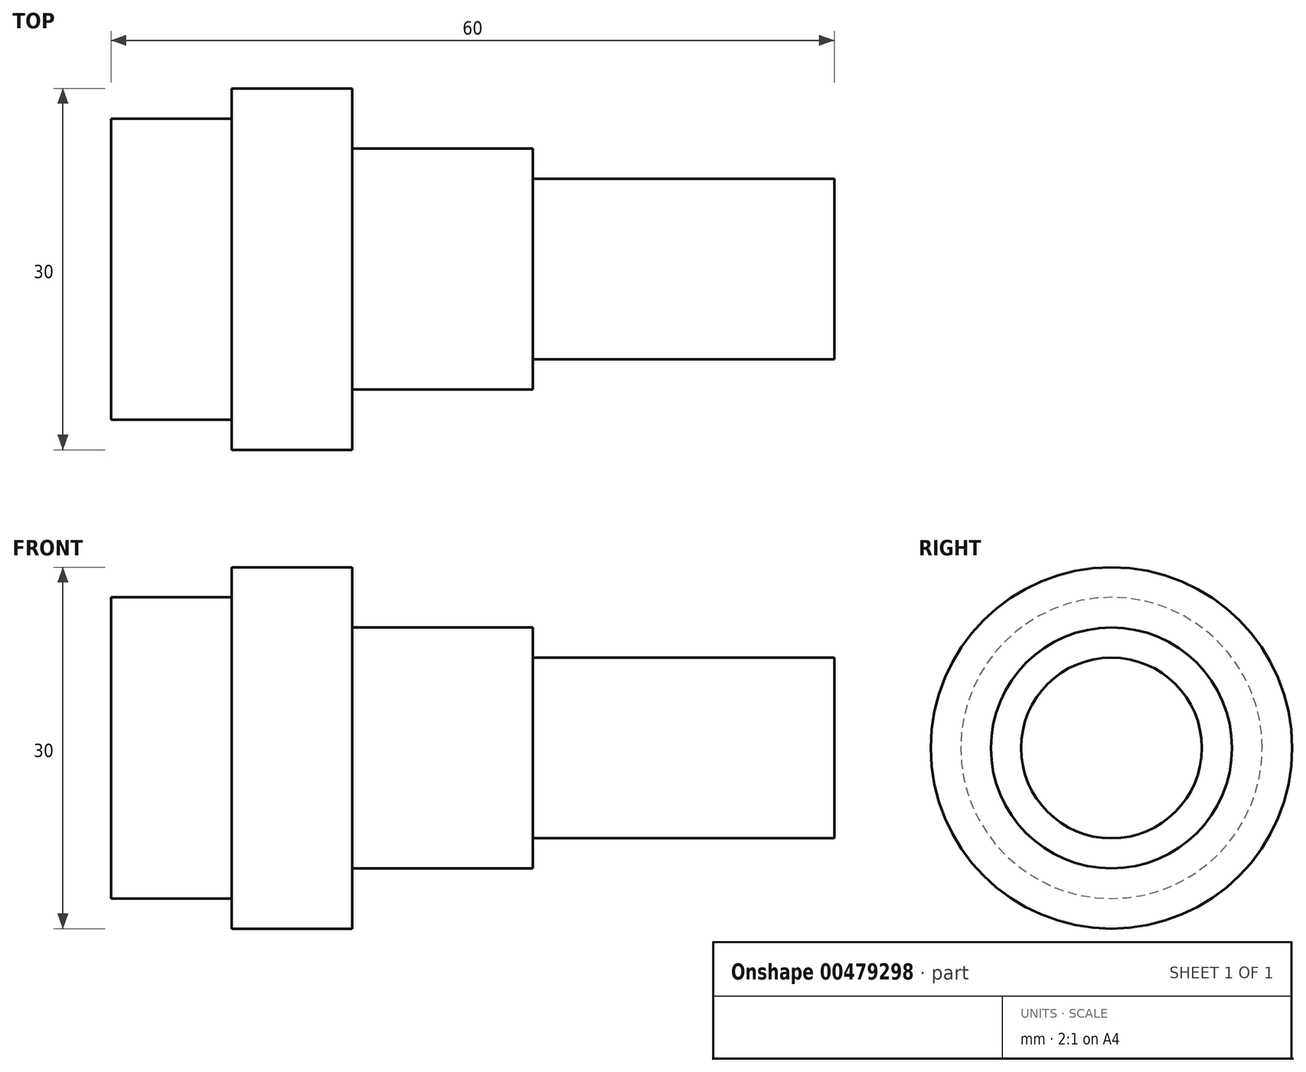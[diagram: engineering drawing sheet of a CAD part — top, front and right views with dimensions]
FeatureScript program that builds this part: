
annotation { "Feature Type Name" : "Feature", "Feature Type Description" : "" }
export const myFeature = defineFeature(function(context is Context, id is Id, definition is map)
    precondition{}
    {
        {
            var Q0;
            Q0=qCreatedBy(makeId("Top.planeOp"),FACE);
            var sketch = newSketch(context, id + "F0", { "sketchPlane" : qUnion([Q0])});
            skLineSegment(sketch, "E0", {"start": v(0, 0) * mm, "end": v(0, 12.5) * mm});
            skLineSegment(sketch, "E1", {"start": v(10, 12.5) * mm, "end": v(10, 15) * mm});
            skLineSegment(sketch, "E2", {"start": v(10, 15) * mm, "end": v(20, 15) * mm});
            skLineSegment(sketch, "E3", {"start": v(20, 15) * mm, "end": v(20, 10) * mm});
            skLineSegment(sketch, "E4", {"start": v(20, 10) * mm, "end": v(35, 10) * mm});
            skLineSegment(sketch, "E5", {"start": v(35, 10) * mm, "end": v(35, 7.5) * mm});
            skLineSegment(sketch, "E6", {"start": v(35, 7.5) * mm, "end": v(60, 7.5) * mm});
            skLineSegment(sketch, "E7", {"start": v(60, 7.5) * mm, "end": v(60, 0) * mm});
            skLineSegment(sketch, "E8", {"start": v(10, 12.5) * mm, "end": v(0, 12.5) * mm});
            skLineSegment(sketch, "E9", {"start": v(0, 0) * mm, "end": v(60, 0) * mm});
            skSolve(sketch);
        }
        {
            var Q0;
            Q0=makeQuery(id+"F0.imprint","IMPRINT",FACE,{"disambiguationData":[TD([[makeQuery(id+"F0.imprint","IMPRINT",EDGE,{"derivedFrom":sQuery(id+"F0.wireOp",EDGE,"E0")}),-1.0]])]});
            var Q1;
            Q1=sQuery(id+"F0.wireOp",EDGE,"E9");
            revolve(context, id + "F1", {"entities" : qUnion([Q0]), "axis" : qUnion([Q1]), "revolveType" : RevolveType.FULL, "oppositeDirection" : true});
        }
    });
